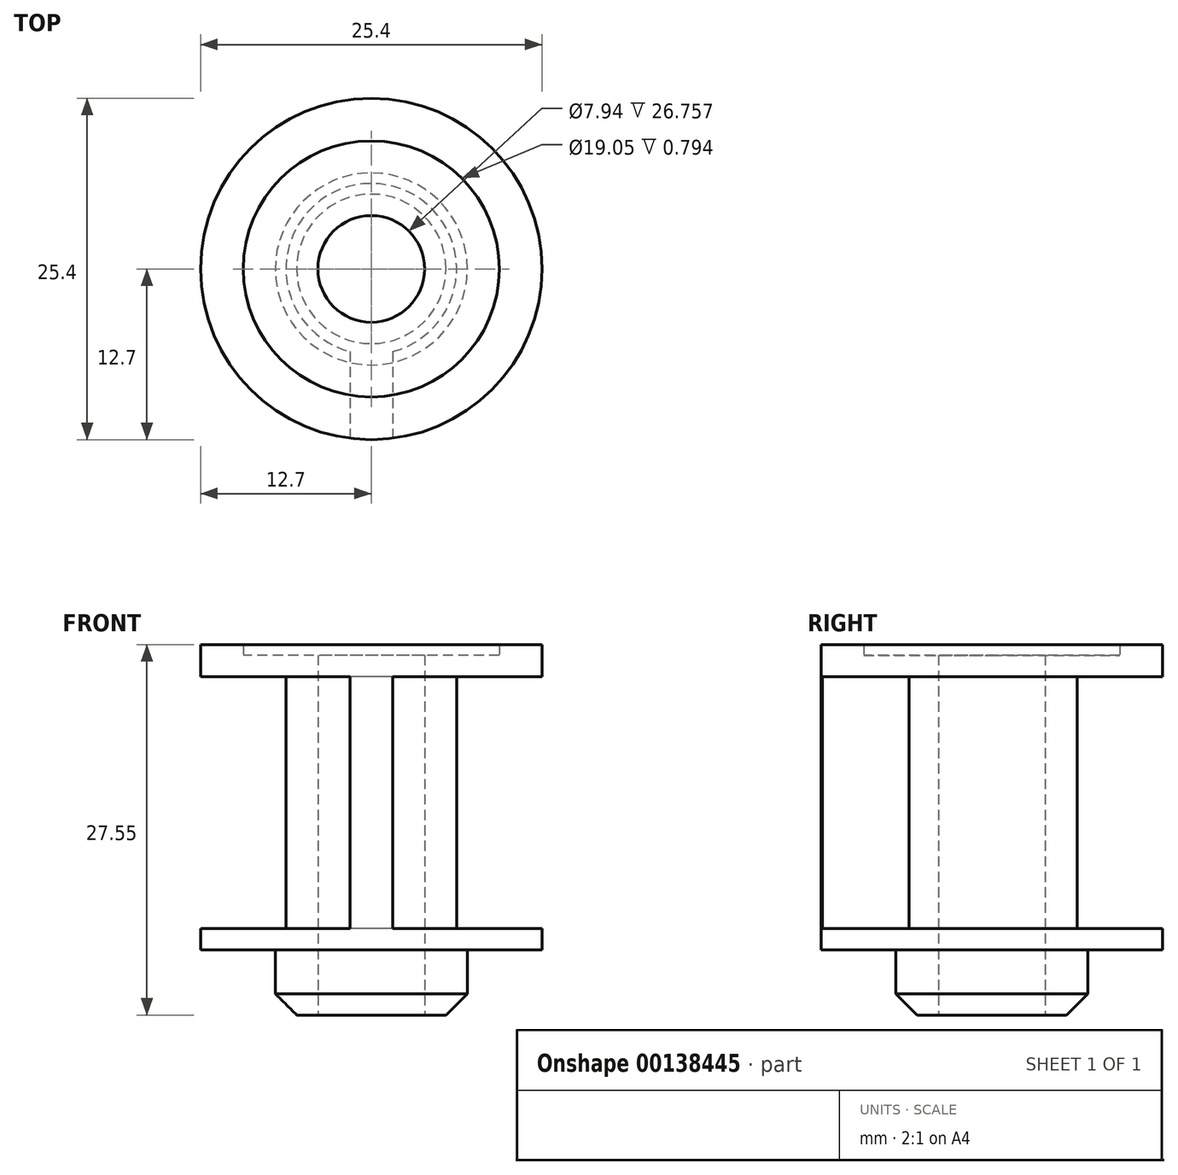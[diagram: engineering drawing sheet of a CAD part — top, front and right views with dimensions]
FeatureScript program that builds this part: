
annotation { "Feature Type Name" : "Feature", "Feature Type Description" : "" }
export const myFeature = defineFeature(function(context is Context, id is Id, definition is map)
    precondition{}
    {
        {
            var Q0;
            Q0=qCreatedBy(makeId("Top.planeOp"),FACE);
            var sketch = newSketch(context, id + "F0", { "sketchPlane" : qUnion([Q0])});
            skCircle(sketch, "E0", {"center": v(0, 0) * mm, "radius": 12.7 * mm});
            skCircle(sketch, "E1", {"center": v(0, 0) * mm, "radius": 3.97 * mm});
            skSolve(sketch);
        }
        {
            var Q0;
            Q0 = qSketchRegion(id + "F0", true);
            extrude(context, id + "F1", {"entities" : qUnion([Q0]), "depth" : 1.59 * mm});
        }
        {
            var Q0;
            Q0=makeQuery(id+"F1.opExtrude","CAP_FACE",FACE,{"disambiguationData":[OSD([sQuery(id+"F0.wireOp",EDGE,"E0")])],"isStart":true});
            var sketch = newSketch(context, id + "F2", { "sketchPlane" : qUnion([Q0])});
            skCircle(sketch, "E2", {"center": v(0, 0) * mm, "radius": 12.7 * mm});
            skCircle(sketch, "E3", {"center": v(0, 0) * mm, "radius": 9.53 * mm});
            skSolve(sketch);
        }
        {
            var Q0;
            Q0 = qSketchRegion(id + "F2", true);
            extrude(context, id + "F3", {"entities" : qUnion([Q0]), "operationType" : NewBodyOperationType.ADD, "depth" : 1 / 812.8 * mm});
        }
        {
            var Q0;
            Q0=makeQuery(id+"F1.opExtrude","CAP_FACE",FACE,{"disambiguationData":[OSD([sQuery(id+"F0.wireOp",EDGE,"E0"),sQuery(id+"F0.wireOp",EDGE,"E1")])],"isStart":false});
            var sketch = newSketch(context, id + "F4", { "sketchPlane" : qUnion([Q0])});
            skCircle(sketch, "E4", {"center": v(0, 0) * mm, "radius": 3.97 * mm});
            skCircle(sketch, "E5", {"center": v(0, 0) * mm, "radius": 6.35 * mm});
            skSolve(sketch);
        }
        {
            var Q0;
            Q0 = qSketchRegion(id + "F4", true);
            extrude(context, id + "F5", {"entities" : qUnion([Q0]), "operationType" : NewBodyOperationType.ADD, "depth" : 18.72 * mm});
        }
        {
            var Q0;
            Q0=makeQuery(id+"F5.opExtrude","CAP_FACE",FACE,{"disambiguationData":[OSD([sQuery(id+"F4.wireOp",EDGE,"E4"),sQuery(id+"F4.wireOp",EDGE,"E5")])],"isStart":false});
            var sketch = newSketch(context, id + "F6", { "sketchPlane" : qUnion([Q0])});
            skCircle(sketch, "E6", {"center": v(0, 0) * mm, "radius": 12.7 * mm});
            skCircle(sketch, "E7", {"center": v(0, 0) * mm, "radius": 3.97 * mm});
            skSolve(sketch);
        }
        {
            var Q0;
            Q0 = qSketchRegion(id + "F6", true);
            extrude(context, id + "F7", {"entities" : qUnion([Q0]), "operationType" : NewBodyOperationType.ADD, "depth" : 1.59 * mm});
        }
        {
            var Q0;
            Q0=makeQuery(id+"F7.opExtrude","CAP_FACE",FACE,{"disambiguationData":[OSD([sQuery(id+"F6.wireOp",EDGE,"E6"),sQuery(id+"F6.wireOp",EDGE,"E7")])],"isStart":false});
            var sketch = newSketch(context, id + "F8", { "sketchPlane" : qUnion([Q0])});
            skCircle(sketch, "E8", {"center": v(0, 0) * mm, "radius": 9.53 * mm});
            skCircle(sketch, "E9", {"center": v(0, 0) * mm, "radius": 12.7 * mm});
            skSolve(sketch);
        }
        {
            var Q0;
            Q0 = qSketchRegion(id + "F8", true);
            extrude(context, id + "F9", {"entities" : qUnion([Q0]), "operationType" : NewBodyOperationType.ADD, "depth" : 0.8 * mm});
        }
        {
            var Q0;
            Q0=makeQuery(id+"F1.opExtrude","CAP_FACE",FACE,{"disambiguationData":[OSD([sQuery(id+"F0.wireOp",EDGE,"E0"),sQuery(id+"F0.wireOp",EDGE,"E1")])],"isStart":false});
            var sketch = newSketch(context, id + "F10", { "sketchPlane" : qUnion([Q0])});
            skLineSegment(sketch, "E10", {"start": v(0, 0) * mm, "end": v(0, -9.37) * mm, "construction": true});
            skLineSegment(sketch, "E11", {"start": v(-1.59, -9.37) * mm, "end": v(1.59, -9.37) * mm, "construction": true});
            skLineSegment(sketch, "E12", {"start": v(1.59, -6.15) * mm, "end": v(1.59, -12.6) * mm});
            skLineSegment(sketch, "E13", {"start": v(-1.59, -6.15) * mm, "end": v(-1.59, -12.6) * mm});
            skArc(sketch, "E14", {"start": v(-1.59, -12.6) * mm, "mid": v(0, -12.7) * mm, "end": v(1.59, -12.6) * mm});
            skArc(sketch, "E15", {"start": v(-1.59, -6.15) * mm, "mid": v(0, -6.35) * mm, "end": v(1.59, -6.15) * mm});
            skSolve(sketch);
        }
        {
            var Q0;
            Q0 = qSketchRegion(id + "F10", true);
            var Q1;
            Q1=makeQuery(id+"F7.opExtrude","CAP_FACE",FACE,{"disambiguationData":[OSD([sQuery(id+"F6.wireOp",EDGE,"E6"),sQuery(id+"F6.wireOp",EDGE,"E7")])],"isStart":true});
            extrude(context, id + "F11", {"entities" : qUnion([Q0]), "operationType" : NewBodyOperationType.ADD, "endBound" : BoundingType.UP_TO_SURFACE, "endBoundEntityFace" : qUnion([Q1]), "depth" : 25.4 * mm});
        }
        {
            var Q0;
            Q0=makeQuery(id+"F1.opExtrude","CAP_FACE",FACE,{"disambiguationData":[OSD([sQuery(id+"F0.wireOp",EDGE,"E0"),sQuery(id+"F0.wireOp",EDGE,"E1")])],"isStart":true});
            var sketch = newSketch(context, id + "F12", { "sketchPlane" : qUnion([Q0])});
            skCircle(sketch, "E16", {"center": v(0, 0) * mm, "radius": 3.97 * mm});
            skCircle(sketch, "E17", {"center": v(0, 0) * mm, "radius": 7.14 * mm});
            skSolve(sketch);
        }
        {
            var Q0;
            Q0 = qSketchRegion(id + "F12", true);
            extrude(context, id + "F13", {"entities" : qUnion([Q0]), "operationType" : NewBodyOperationType.ADD, "depth" : 4.86 * mm});
        }
        {
            var Q0;
            Q0=makeQuery(id+"F13.opExtrude","CAP_EDGE",EDGE,{"disambiguationData":[OSD([sQuery(id+"F12.wireOp",EDGE,"E17")])],"isStart":false});
            chamfer(context, id + "F14", {"entities" : qUnion([Q0]), "width" : 1.59 * mm, "tangentPropagation" : true});
        }
    });
